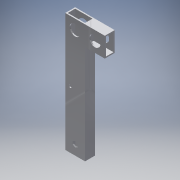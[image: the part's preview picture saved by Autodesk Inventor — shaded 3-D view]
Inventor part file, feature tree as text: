
AUTODESK INVENTOR PART (.ipt)
format: ipt  version: 2016 (Build 200138000, 138)  size: 167,936 bytes
history: native  units: in
note: dims shown in document units (in); Inventor stores cm internally (conversion verified against a paired STEP export)
features: extrude x6, sketch x6
ambient origin geometry x8: Origin, YZ Plane, XZ Plane, XY Plane, X Axis, Y Axis, Z Axis, Center Point
bodies: Solid1 (feature_tree)
feature tree (12):
  extrude  "Extrusion1"  Depth=1.0in
  extrude  "Extrusion2"  Depth=0.1253in
  extrude  "Extrusion3"  Depth=0.125in
  extrude  "Extrusion4"  Depth=2.0in
  extrude  "Extrusion5"  Depth=0.125in
  extrude  "Extrusion6"  Depth=1.0in
  sketch  "Sketch1"  dims[d0=2.0in d1=1.0in]
  sketch  "Sketch2"  dims[d2=0.125in d3=0.1253in]
  sketch  "Sketch3"  dims[d4=0.125in d5=0.125in]
  sketch  "Sketch4"  dims[d6=12.0in d7=0.0in d8=2.0in]
  sketch  "Sketch5"  dims[d9=0.125in d10=0.125in]
  sketch  "Sketch6"  dims[d11=2.0in d12=0.0in d13=1.0in d14=1.125in d15=2.0in d16=0.0in d17=1.0in d18=1.125in d19=2.0in d20=0.0in d21=1.0in d22=1.125in d23=1.0in d24=1.0in d25=0.0in d26=1.0in d27=1.0in d28=0.75in d29=0.5in d30=1.0in d31=0.0in d32=0.2656in d33=6.1875in d34=0.5in]
